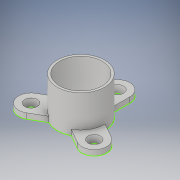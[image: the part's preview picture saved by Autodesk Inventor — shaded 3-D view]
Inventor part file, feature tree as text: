
AUTODESK INVENTOR PART (.ipt)
format: ipt  version: 2018 (Build 220112000, 112)  size: 191,488 bytes
history: native  units: in
note: dims shown in document units (in); Inventor stores cm internally (conversion verified against a paired STEP export)
features: sketch x5, extrude x4, plane x3, revolve x3, other x2, projected_geometry x1
ambient origin geometry x8: Origin, YZ Plane, XZ Plane, XY Plane, X Axis, Y Axis, Z Axis, Center Point
bodies: Solid1 (feature_tree)
feature tree (18):
  sketch  "Sketch1"  dims[d13=1.163in d14=0.0in d15=0.166in d16=0.0in]
  extrude  "Extrusion1"  Depth=0.166in TaperAngle=0.0deg
  extrude  "Extrusion2"  Depth=0.166in TaperAngle=0.0deg
  extrude  "Extrusion3"  TaperAngle=90.0deg  [1 undecoded]
  extrude  "Extrusion4"  TaperAngle=90.0deg  [1 undecoded]
  sketch  "Sketch2"  dims[d17=0.166in d18=0.0in d19=0.166in d20=0.0in]
  plane  "Work Plane1"
  sketch  "Sketch3"  dims[d23=-0.384in d24=90.0deg]
  other  "Work Axis1"
  revolve  "Revolution1"  Angle=90.0deg
  other  "Work Axis2"
  plane  "Work Plane2"
  revolve  "Revolution2"  [1 undecoded]
  plane  "Work Plane3"
  revolve  "Revolution3"  [1 undecoded]
  projected_geometry  "Projected Loop1"
  sketch  "Sketch4"  dims[d25=120.0deg d26=90.0deg]
  sketch  "Sketch5"  dims[d27=120.0deg d28=90.0deg]
note: 4 required parameter values undecoded (feature->parameter linkage not recoverable at this tier; creation-order binding heuristic only, values carry confidence <= 0.55)
